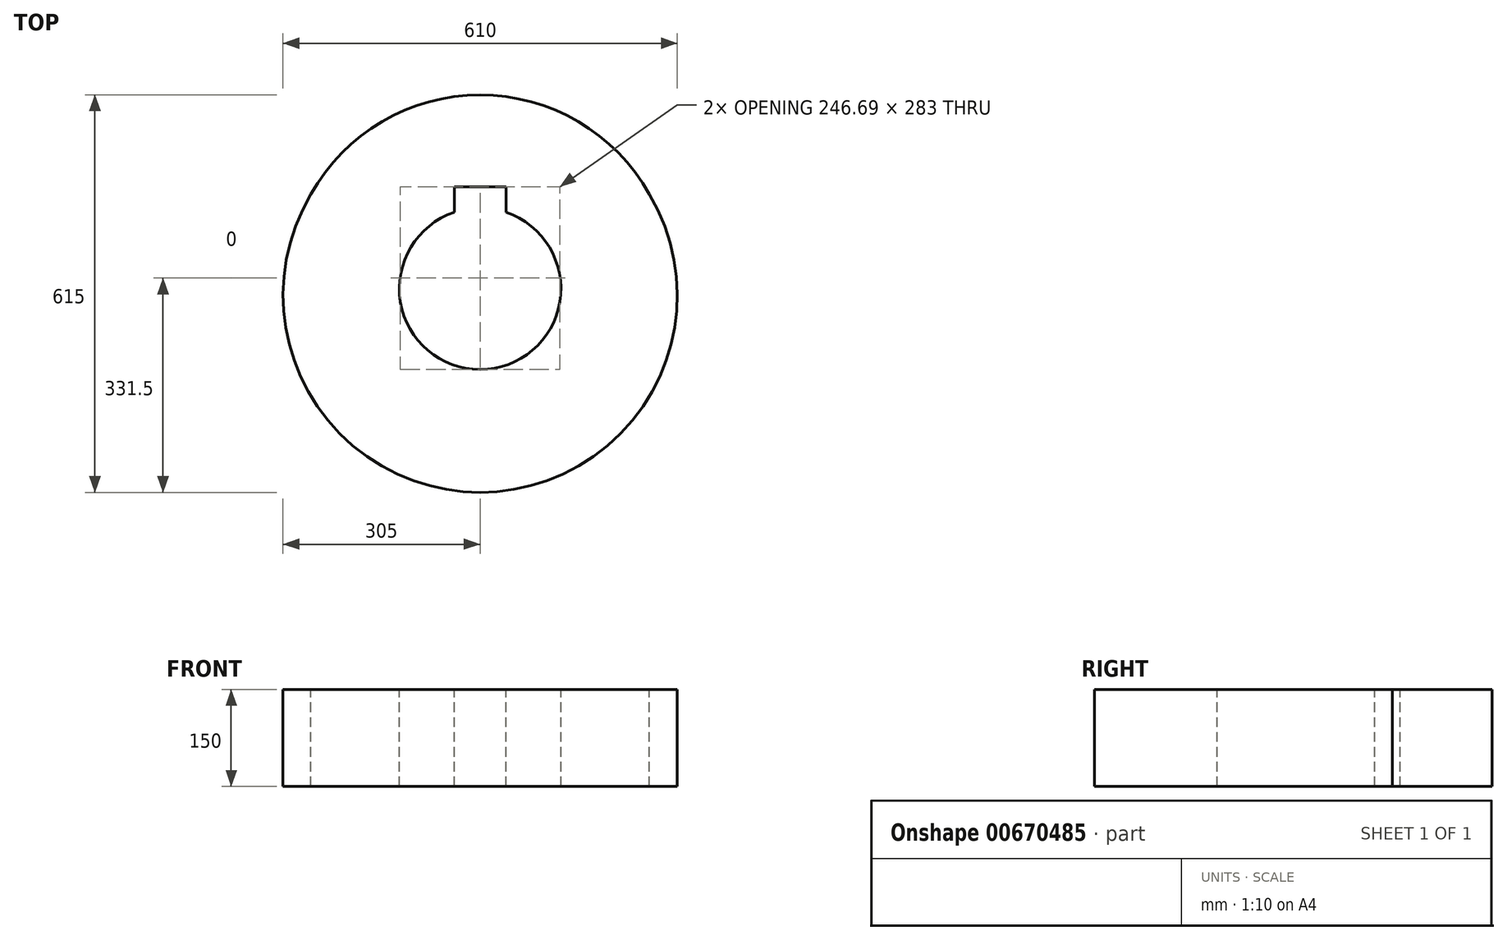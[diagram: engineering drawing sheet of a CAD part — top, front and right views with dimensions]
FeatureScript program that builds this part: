
annotation { "Feature Type Name" : "Feature", "Feature Type Description" : "" }
export const myFeature = defineFeature(function(context is Context, id is Id, definition is map)
    precondition{}
    {
        {
            var Q0;
            Q0=qCreatedBy(makeId("Top.planeOp"),FACE);
            var sketch = newSketch(context, id + "F0", { "sketchPlane" : qUnion([Q0])});
            skCircle(sketch, "E0", {"center": v(0, 0) * mm, "radius": 300 * mm});
            skCircle(sketch, "E1", {"center": v(0, -10) * mm, "radius": 305 * mm});
            skSolve(sketch);
        }
        {
            var Q0;
            Q0 = qSketchRegion(id + "F0", true);
            var Q1;
            {var subQ0=sQuery(id+"F0.wireOp",EDGE,"E1");var subQ1=sQuery(id+"F0.wireOp",EDGE,"E0");var subQ2=makeQuery(id+"F0.imprint","INTERSECT",VERTEX,{"disambiguationData":[OD(0.0)],"derivedFrom":[subQ1,subQ0]});Q1=makeQuery(id+"F0.imprint","IMPRINT",FACE,{"disambiguationData":[TD([[makeQuery(id+"F0.imprint","IMPRINT",EDGE,{"disambiguationData":[TD([[subQ2,1.0]])],"derivedFrom":subQ1}),1.0]])]});}
            extrude(context, id + "F1", {"entities" : qUnion([Q0, Q1]), "oppositeDirection" : true, "depth" : 150 * mm, "offsetDistance" : 25.4 * mm});
        }
        {
            var Q0;
            Q0=qCreatedBy(makeId("Top.planeOp"),FACE);
            var sketch = newSketch(context, id + "F2", { "sketchPlane" : qUnion([Q0])});
            skCircle(sketch, "E2", {"center": v(0, 0) * mm, "radius": 125 * mm});
            skLineSegment(sketch, "E3.bottom", {"start": v(40, 0) * mm, "end": v(-40, 0) * mm});
            skLineSegment(sketch, "E3.top", {"start": v(40, 158) * mm, "end": v(-40, 158) * mm});
            skLineSegment(sketch, "E3.left", {"start": v(40, 0) * mm, "end": v(40, 158) * mm});
            skLineSegment(sketch, "E3.right", {"start": v(-40, 0) * mm, "end": v(-40, 158) * mm});
            skSolve(sketch);
        }
        {
            var Q0;
            Q0 = qSketchRegion(id + "F2", true);
            extrude(context, id + "F3", {"entities" : qUnion([Q0]), "operationType" : NewBodyOperationType.REMOVE, "oppositeDirection" : true, "depth" : 264.16 * mm, "offsetDistance" : 25.4 * mm});
        }
    });
